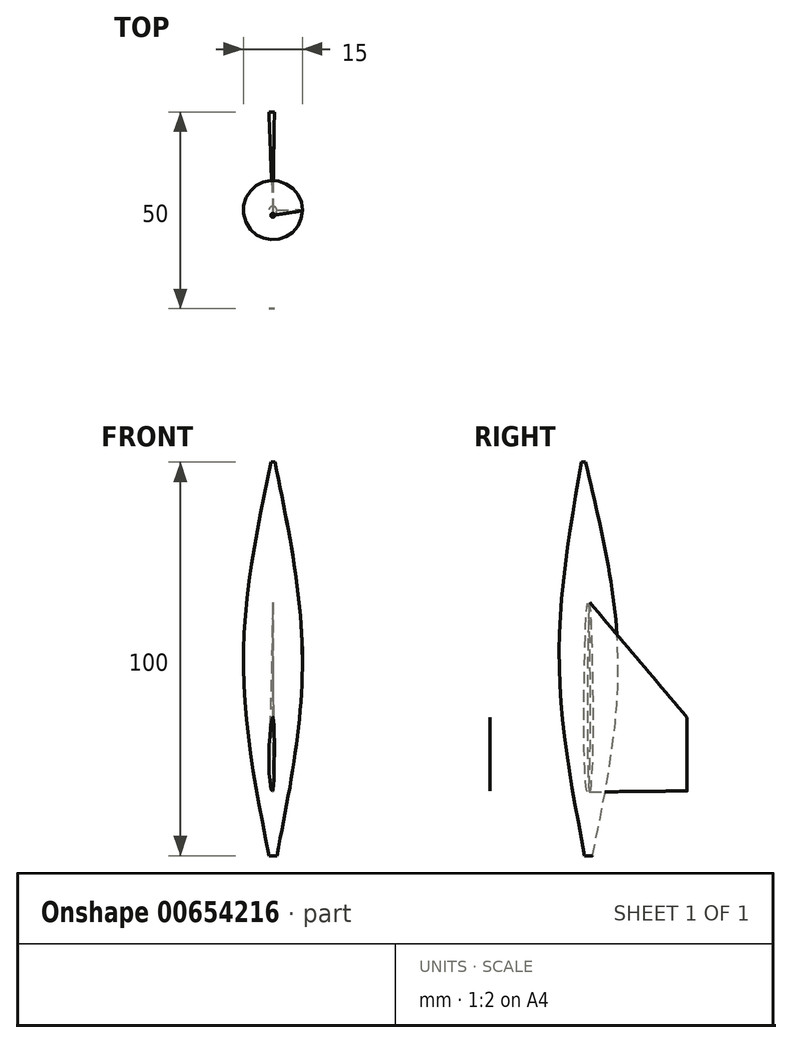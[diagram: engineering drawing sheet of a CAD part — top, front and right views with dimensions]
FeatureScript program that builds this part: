
annotation { "Feature Type Name" : "Feature", "Feature Type Description" : "" }
export const myFeature = defineFeature(function(context is Context, id is Id, definition is map)
    precondition{}
    {
        {
            var Q0;
            Q0=qCreatedBy(makeId("Top.planeOp"),FACE);
            var sketch = newSketch(context, id + "F0", { "sketchPlane" : qUnion([Q0])});
            skCircle(sketch, "E0", {"center": v(0, 0) * mm, "radius": 1 * mm});
            skSolve(sketch);
        }
        {
            var Q0;
            Q0=qCreatedBy(makeId("Top.planeOp"),FACE);
            cPlane(context, id + "F1", {"entities" : qUnion([Q0]), "cplaneType" : CPlaneType.OFFSET, "offset" : 50 * mm, "width" : 150 * mm, "height" : 150 * mm});
        }
        {
            var Q0;
            Q0=qCreatedBy(makeId("Top.planeOp"),FACE);
            cPlane(context, id + "F2", {"entities" : qUnion([Q0]), "cplaneType" : CPlaneType.OFFSET, "offset" : 100 * mm, "width" : 150 * mm, "height" : 150 * mm});
        }
        {
            var Q0;
            Q0=qCreatedBy(id+"F1.planeOp",FACE);
            var sketch = newSketch(context, id + "F3", { "sketchPlane" : qUnion([Q0])});
            skCircle(sketch, "E1", {"center": v(0, 0) * mm, "radius": 7.5 * mm});
            skSolve(sketch);
        }
        {
            var Q0;
            Q0=qCreatedBy(id+"F2.planeOp",FACE);
            var sketch = newSketch(context, id + "F4", { "sketchPlane" : qUnion([Q0])});
            skCircle(sketch, "E2", {"center": v(0, -1.3) * mm, "radius": 0.5 * mm});
            skSolve(sketch);
        }
        {
            var Q0;
            Q0=qSketchRegion(id+"F0",true);
            var Q1;
            Q1=qSketchRegion(id+"F3",true);
            var Q2;
            Q2=qSketchRegion(id+"F4",true);
            loft(context, id + "F5", {"sheetProfilesArray" : [{ "sheetProfileEntities" : qUnion([Q0]) }, { "sheetProfileEntities" : qUnion([Q1]) }, { "sheetProfileEntities" : qUnion([Q2]) }]});
        }
        {
            var Q0;
            Q0=qCreatedBy(makeId("Right.planeOp"),FACE);
            var sketch = newSketch(context, id + "F6", { "sketchPlane" : qUnion([Q0])});
            skFitSpline(sketch, "E3", {"points": [v(0.26, 16.2) * mm, v(1.12, 26.03) * mm, v(0.3, 64.3) * mm, v(-0.32, 32.4) * mm, v(0.26, 16.2) * mm]});
            skSolve(sketch);
        }
        {
            var Q0;
            Q0=qCreatedBy(makeId("Front.planeOp"),FACE);
            cPlane(context, id + "F7", {"entities" : qUnion([Q0]), "cplaneType" : CPlaneType.OFFSET, "offset" : 25 * mm, "oppositeDirection" : true, "width" : 150 * mm, "height" : 150 * mm});
        }
        {
            var Q0;
            Q0=qCreatedBy(id+"F7.planeOp",FACE);
            var sketch = newSketch(context, id + "F8", { "sketchPlane" : qUnion([Q0])});
            skFitSpline(sketch, "E4", {"points": [v(-0.17, 16.46) * mm, v(-1.03, 23.85) * mm, v(0, 35.2) * mm, v(0.35, 23.33) * mm, v(-0.17, 16.46) * mm]});
            skSolve(sketch);
        }
        {
            var Q0;
            Q0=qSketchRegion(id+"F6",true);
            var Q1;
            Q1=qSketchRegion(id+"F8",true);
            loft(context, id + "F9", {"sheetProfilesArray" : [{ "sheetProfileEntities" : qUnion([Q0]) }, { "sheetProfileEntities" : qUnion([Q1]) }]});
        }
        {
            var Q0;
            Q0=makeQuery(id+"F9.opLoft","SWEPT_BODY",BODY,{"disambiguationData":[OSD([makeQuery(id+"F6.imprint","IMPRINT",FACE,{"disambiguationData":[TD([[makeQuery(id+"F6.imprint","IMPRINT",EDGE,{"derivedFrom":sQuery(id+"F6.wireOp",EDGE,"E3")}),1.0]])]}),makeQuery(id+"F8.imprint","IMPRINT",FACE,{"disambiguationData":[TD([[makeQuery(id+"F8.imprint","IMPRINT",EDGE,{"derivedFrom":sQuery(id+"F8.wireOp",EDGE,"E4")}),-1.0]])]})])]});
            var Q1;
            Q1=qCreatedBy(makeId("Front.planeOp"),FACE);
            mirror(context, id + "F10", {"entities" : qUnion([Q0]), "mirrorPlane" : qUnion([Q1])});
        }
    });
